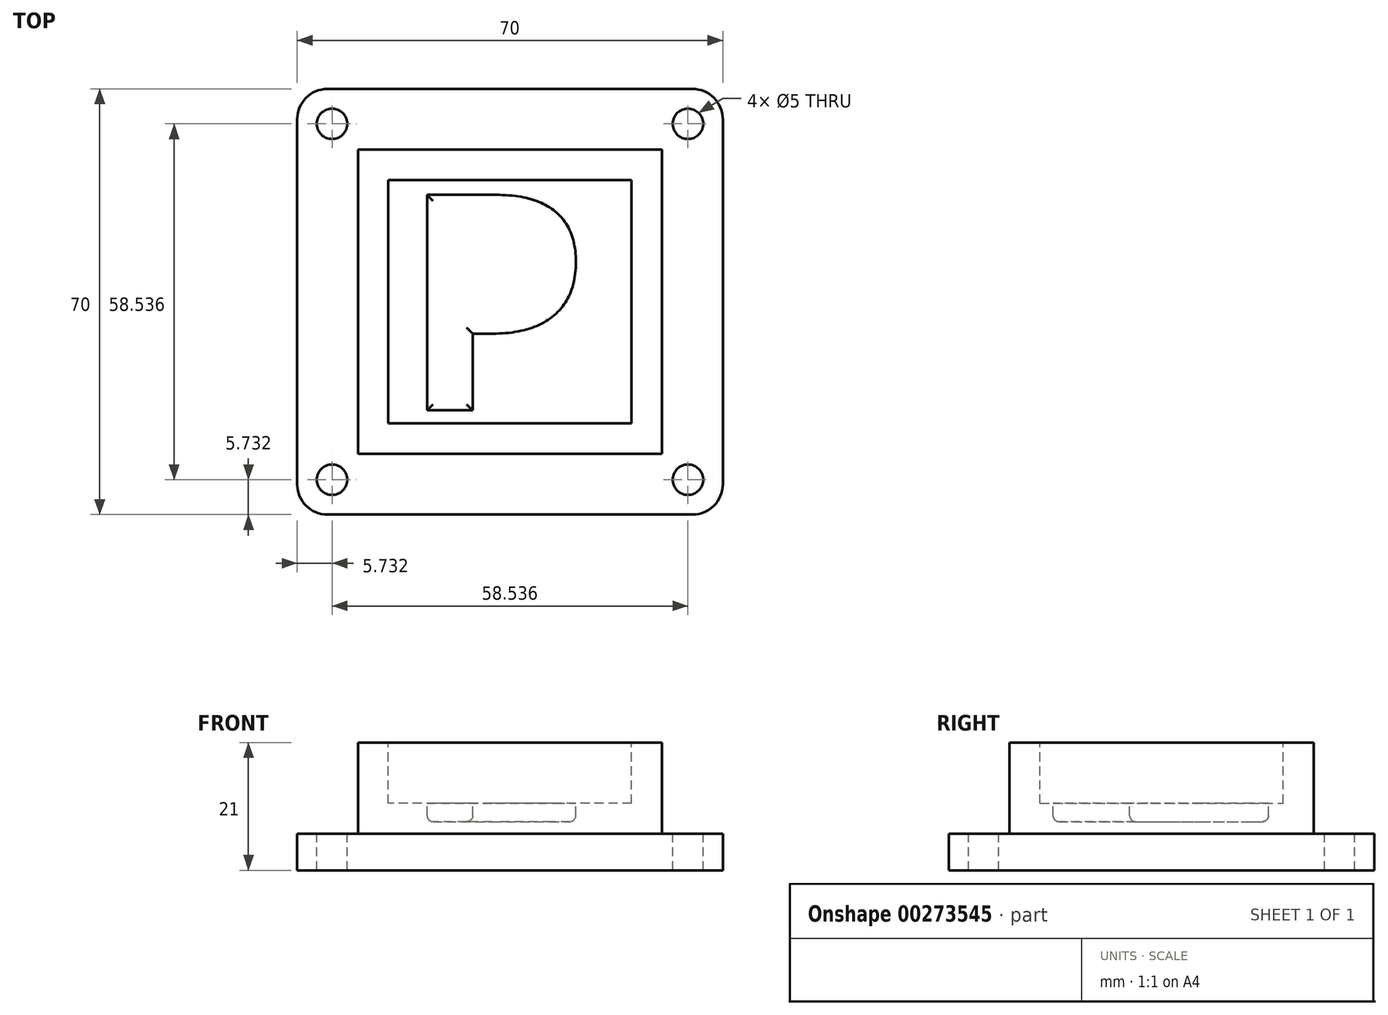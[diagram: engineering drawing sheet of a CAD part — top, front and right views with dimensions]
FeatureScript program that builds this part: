
annotation { "Feature Type Name" : "Feature", "Feature Type Description" : "" }
export const myFeature = defineFeature(function(context is Context, id is Id, definition is map)
    precondition{}
    {
        {
            var Q0;
            Q0=qCreatedBy(makeId("Top.planeOp"),FACE);
            var sketch = newSketch(context, id + "F0", { "sketchPlane" : qUnion([Q0])});
            skLineSegment(sketch, "E0.bottom", {"start": v(35, -35) * mm, "end": v(-35, -35) * mm});
            skLineSegment(sketch, "E0.top", {"start": v(35, 35) * mm, "end": v(-35, 35) * mm});
            skLineSegment(sketch, "E0.left", {"start": v(35, -35) * mm, "end": v(35, 35) * mm});
            skLineSegment(sketch, "E0.right", {"start": v(-35, -35) * mm, "end": v(-35, 35) * mm});
            skPoint(sketch, "E0.middle", {"position": v(0, 0) * mm});
            skSolve(sketch);
        }
        {
            var Q0;
            Q0=makeQuery(id+"F0.imprint","IMPRINT",FACE,{"disambiguationData":[TD([[makeQuery(id+"F0.imprint","IMPRINT",EDGE,{"derivedFrom":sQuery(id+"F0.wireOp",EDGE,"E0.bottom")}),-1.0]])]});
            extrude(context, id + "F1", {"entities" : qUnion([Q0]), "depth" : 6 * mm});
        }
        {
            var Q0;
            Q0=makeQuery(id+"F1.opExtrude","CAP_FACE",FACE,{"disambiguationData":[OSD([sQuery(id+"F0.wireOp",EDGE,"E0.bottom"),sQuery(id+"F0.wireOp",EDGE,"E0.top"),sQuery(id+"F0.wireOp",EDGE,"E0.left"),sQuery(id+"F0.wireOp",EDGE,"E0.right")])],"isStart":false});
            var sketch = newSketch(context, id + "F2", { "sketchPlane" : qUnion([Q0])});
            skLineSegment(sketch, "E1.bottom", {"start": v(25, -25) * mm, "end": v(-25, -25) * mm});
            skLineSegment(sketch, "E1.top", {"start": v(25, 25) * mm, "end": v(-25, 25) * mm});
            skLineSegment(sketch, "E1.left", {"start": v(25, -25) * mm, "end": v(25, 25) * mm});
            skLineSegment(sketch, "E1.right", {"start": v(-25, -25) * mm, "end": v(-25, 25) * mm});
            skPoint(sketch, "E1.middle", {"position": v(0, 0) * mm});
            skSolve(sketch);
        }
        {
            var Q0;
            Q0=makeQuery(id+"F2.imprint","IMPRINT",FACE,{"disambiguationData":[TD([[makeQuery(id+"F2.imprint","IMPRINT",EDGE,{"derivedFrom":sQuery(id+"F2.wireOp",EDGE,"E1.bottom")}),-1.0]])]});
            extrude(context, id + "F3", {"entities" : qUnion([Q0]), "operationType" : NewBodyOperationType.ADD, "depth" : 15 * mm});
        }
        {
            var Q0;
            Q0=makeQuery(id+"F1.opExtrude","SWEPT_EDGE",EDGE,{"disambiguationData":[OSD([sQuery(id+"F0.wireOp",EDGE,"E0.top"),sQuery(id+"F0.wireOp",EDGE,"E0.right")])]});
            var Q1;
            Q1=makeQuery(id+"F1.opExtrude","SWEPT_EDGE",EDGE,{"disambiguationData":[OSD([sQuery(id+"F0.wireOp",EDGE,"E0.top"),sQuery(id+"F0.wireOp",EDGE,"E0.left")])]});
            var Q2;
            Q2=makeQuery(id+"F1.opExtrude","SWEPT_EDGE",EDGE,{"disambiguationData":[OSD([sQuery(id+"F0.wireOp",EDGE,"E0.bottom"),sQuery(id+"F0.wireOp",EDGE,"E0.left")])]});
            var Q3;
            Q3=makeQuery(id+"F1.opExtrude","SWEPT_EDGE",EDGE,{"disambiguationData":[OSD([sQuery(id+"F0.wireOp",EDGE,"E0.bottom"),sQuery(id+"F0.wireOp",EDGE,"E0.right")])]});
            fillet(context, id + "F4", {"entities" : qUnion([Q0, Q1, Q2, Q3]), "radius" : 5 * mm, "tangentPropagation" : true, "allowEdgeOverflow" : false});
        }
        {
            var Q0;
            Q0=makeQuery(id+"F1.opExtrude","CAP_FACE",FACE,{"disambiguationData":[OSD([sQuery(id+"F0.wireOp",EDGE,"E0.bottom"),sQuery(id+"F0.wireOp",EDGE,"E0.top"),sQuery(id+"F0.wireOp",EDGE,"E0.left"),sQuery(id+"F0.wireOp",EDGE,"E0.right")])],"isStart":false});
            var sketch = newSketch(context, id + "F5", { "sketchPlane" : qUnion([Q0])});
            skLineSegment(sketch, "E2.0", {"start": v(-35, -30) * mm, "end": v(-35, 30) * mm, "construction": true});
            skPoint(sketch, "E3.0", {"position": v(-33.54, 33.54) * mm});
            skArc(sketch, "E4.0", {"start": v(-30, 35) * mm, "mid": v(-33.54, 33.54) * mm, "end": v(-35, 30) * mm});
            skLineSegment(sketch, "E5.0", {"start": v(30, 35) * mm, "end": v(-30, 35) * mm, "construction": true});
            skLineSegment(sketch, "E6.0", {"start": v(35, -30) * mm, "end": v(35, 30) * mm, "construction": true});
            skArc(sketch, "E7.0", {"start": v(30, -35) * mm, "mid": v(33.54, -33.54) * mm, "end": v(35, -30) * mm, "construction": true});
            skLineSegment(sketch, "E8.0", {"start": v(30, -35) * mm, "end": v(-30, -35) * mm, "construction": true});
            skArc(sketch, "E9.0", {"start": v(-35, -30) * mm, "mid": v(-33.54, -33.54) * mm, "end": v(-30, -35) * mm, "construction": true});
            skPoint(sketch, "E10.0", {"position": v(33.54, 33.54) * mm});
            skPoint(sketch, "E11", {"position": v(-33.54, -33.54) * mm});
            skPoint(sketch, "E12", {"position": v(33.54, -33.54) * mm});
            skLineSegment(sketch, "E13", {"start": v(-33.54, 33.54) * mm, "end": v(-25, 25) * mm, "construction": true});
            skLineSegment(sketch, "E14", {"start": v(25, 25) * mm, "end": v(33.54, 33.54) * mm, "construction": true});
            skLineSegment(sketch, "E15", {"start": v(25, -25) * mm, "end": v(33.54, -33.54) * mm, "construction": true});
            skLineSegment(sketch, "E16", {"start": v(-25, -25) * mm, "end": v(-33.54, -33.54) * mm, "construction": true});
            skPoint(sketch, "E17", {"position": v(-29.27, 29.27) * mm});
            skPoint(sketch, "E18", {"position": v(29.27, 29.27) * mm});
            skPoint(sketch, "E19", {"position": v(29.27, -29.27) * mm});
            skPoint(sketch, "E20", {"position": v(-29.27, -29.27) * mm});
            skCircle(sketch, "E21", {"center": v(-29.27, 29.27) * mm, "radius": 2.5 * mm});
            skCircle(sketch, "E22", {"center": v(29.27, 29.27) * mm, "radius": 2.5 * mm});
            skCircle(sketch, "E23", {"center": v(29.27, -29.27) * mm, "radius": 2.5 * mm});
            skCircle(sketch, "E24", {"center": v(-29.27, -29.27) * mm, "radius": 2.5 * mm});
            skSolve(sketch);
        }
        {
            var Q0;
            Q0=makeQuery(id+"F5.imprint","IMPRINT",FACE,{"disambiguationData":[TD([[makeQuery(id+"F5.imprint","IMPRINT",EDGE,{"derivedFrom":sQuery(id+"F5.wireOp",EDGE,"E21")}),1.0]])]});
            var Q1;
            Q1=makeQuery(id+"F5.imprint","IMPRINT",FACE,{"disambiguationData":[TD([[makeQuery(id+"F5.imprint","IMPRINT",EDGE,{"derivedFrom":sQuery(id+"F5.wireOp",EDGE,"E22")}),1.0]])]});
            var Q2;
            Q2=makeQuery(id+"F5.imprint","IMPRINT",FACE,{"disambiguationData":[TD([[makeQuery(id+"F5.imprint","IMPRINT",EDGE,{"derivedFrom":sQuery(id+"F5.wireOp",EDGE,"E23")}),1.0]])]});
            var Q3;
            Q3=makeQuery(id+"F5.imprint","IMPRINT",FACE,{"disambiguationData":[TD([[makeQuery(id+"F5.imprint","IMPRINT",EDGE,{"derivedFrom":sQuery(id+"F5.wireOp",EDGE,"E24")}),1.0]])]});
            extrude(context, id + "F6", {"entities" : qUnion([Q0, Q1, Q2, Q3]), "operationType" : NewBodyOperationType.REMOVE, "oppositeDirection" : true, "depth" : 25 * mm});
        }
        {
            var Q0;
            Q0=makeQuery(id+"F3.opExtrude","CAP_FACE",FACE,{"disambiguationData":[OSD([sQuery(id+"F2.wireOp",EDGE,"E1.bottom"),sQuery(id+"F2.wireOp",EDGE,"E1.top"),sQuery(id+"F2.wireOp",EDGE,"E1.left"),sQuery(id+"F2.wireOp",EDGE,"E1.right")])],"isStart":false});
            var sketch = newSketch(context, id + "F7", { "sketchPlane" : qUnion([Q0])});
            skSolve(sketch);
        }
        {
            var Q0;
            Q0=makeQuery(id+"F7.imprint","IMPRINT",FACE,{"disambiguationData":[TD([[makeQuery(id+"F7.imprint","IMPRINT",EDGE,{"derivedFrom":makeQuery(id+"F3.opExtrude","CAP_EDGE",EDGE,{"disambiguationData":[OSD([sQuery(id+"F2.wireOp",EDGE,"E1.bottom")])],"isStart":false})}),-1.0]])]});
            var sketch = newSketch(context, id + "F8", { "sketchPlane" : qUnion([Q0])});
            skLineSegment(sketch, "E25.bottom", {"start": v(20, -20) * mm, "end": v(-20, -20) * mm});
            skLineSegment(sketch, "E25.top", {"start": v(20, 20) * mm, "end": v(-20, 20) * mm});
            skLineSegment(sketch, "E25.left", {"start": v(20, -20) * mm, "end": v(20, 20) * mm});
            skLineSegment(sketch, "E25.right", {"start": v(-20, -20) * mm, "end": v(-20, 20) * mm});
            skPoint(sketch, "E25.middle", {"position": v(0, 0) * mm});
            skText(sketch, "E26", { "text": "P", "fontName": "OpenSans-Bold.ttf"});
            const initialGuessF8  = {"E26": [-0.0181, -0.01785, 1, 0, 0.03574]};
            skSetInitialGuess(sketch, initialGuessF8);
            skSolve(sketch);
        }
        {
            var Q0;
            Q0=makeQuery(id+"F8.imprint","IMPRINT",FACE,{"disambiguationData":[TD([[makeQuery(id+"F8.imprint","IMPRINT",EDGE,{"derivedFrom":sQuery(id+"F8.wireOp",EDGE,"E25.bottom")}),-1.0]])]});
            extrude(context, id + "F9", {"entities" : qUnion([Q0]), "operationType" : NewBodyOperationType.REMOVE, "oppositeDirection" : true, "depth" : 10 * mm});
        }
        {
            var Q0;
            Q0=makeQuery(id+"F8.imprint","IMPRINT",FACE,{"disambiguationData":[TD([[makeQuery(id+"F8.imprint","IMPRINT",EDGE,{"derivedFrom":sQuery(id+"F8.wireOp",EDGE,"E26.sketch_text.stroke-0")}),-1.0]])]});
            extrude(context, id + "F10", {"entities" : qUnion([Q0]), "operationType" : NewBodyOperationType.REMOVE, "oppositeDirection" : true, "depth" : 13 * mm});
        }
        {
            var Q0;
            Q0=makeQuery(id+"F8.imprint","IMPRINT",FACE,{"disambiguationData":[TD([[makeQuery(id+"F8.imprint","IMPRINT",EDGE,{"derivedFrom":sQuery(id+"F8.wireOp",EDGE,"E26.sketch_text.stroke-0")}),1.0]])]});
            extrude(context, id + "F11", {"entities" : qUnion([Q0]), "operationType" : NewBodyOperationType.REMOVE, "oppositeDirection" : true, "depth" : 13 * mm});
        }
        {
            var Q0;
            Q0=makeQuery(id+"F10.boolean.opBoolean","COPY",EDGE,{"derivedFrom":makeQuery(id+"F10.opExtrude","CAP_EDGE",EDGE,{"disambiguationData":[OSD([sQuery(id+"F8.wireOp",EDGE,"E26.sketch_text.stroke-12")])],"isStart":false})});
            var Q1;
            Q1=makeQuery(id+"F10.boolean.opBoolean","COPY",EDGE,{"derivedFrom":makeQuery(id+"F10.opExtrude","CAP_EDGE",EDGE,{"disambiguationData":[OSD([sQuery(id+"F8.wireOp",EDGE,"E26.sketch_text.stroke-13")])],"isStart":false})});
            var Q2;
            Q2=makeQuery(id+"F10.boolean.opBoolean","COPY",EDGE,{"derivedFrom":makeQuery(id+"F10.opExtrude","CAP_EDGE",EDGE,{"disambiguationData":[OSD([sQuery(id+"F8.wireOp",EDGE,"E26.sketch_text.stroke-14")])],"isStart":false})});
            var Q3;
            Q3=makeQuery(id+"F10.boolean.opBoolean","COPY",EDGE,{"derivedFrom":makeQuery(id+"F10.opExtrude","CAP_EDGE",EDGE,{"disambiguationData":[OSD([sQuery(id+"F8.wireOp",EDGE,"E26.sketch_text.stroke-15")])],"isStart":false})});
            var Q4;
            Q4=makeQuery(id+"F10.boolean.opBoolean","COPY",EDGE,{"derivedFrom":makeQuery(id+"F10.opExtrude","CAP_EDGE",EDGE,{"disambiguationData":[OSD([sQuery(id+"F8.wireOp",EDGE,"E26.sketch_text.stroke-7")])],"isStart":false})});
            var Q5;
            Q5=makeQuery(id+"F10.boolean.opBoolean","COPY",EDGE,{"derivedFrom":makeQuery(id+"F10.opExtrude","CAP_EDGE",EDGE,{"disambiguationData":[OSD([sQuery(id+"F8.wireOp",EDGE,"E26.sketch_text.stroke-8")])],"isStart":false})});
            var Q6;
            Q6=makeQuery(id+"F10.boolean.opBoolean","COPY",EDGE,{"derivedFrom":makeQuery(id+"F10.opExtrude","CAP_EDGE",EDGE,{"disambiguationData":[OSD([sQuery(id+"F8.wireOp",EDGE,"E26.sketch_text.stroke-9")])],"isStart":false})});
            var Q7;
            Q7=makeQuery(id+"F10.boolean.opBoolean","COPY",EDGE,{"derivedFrom":makeQuery(id+"F10.opExtrude","CAP_EDGE",EDGE,{"disambiguationData":[OSD([sQuery(id+"F8.wireOp",EDGE,"E26.sketch_text.stroke-10")])],"isStart":false})});
            var Q8;
            Q8=makeQuery(id+"F10.boolean.opBoolean","COPY",EDGE,{"derivedFrom":makeQuery(id+"F10.opExtrude","CAP_EDGE",EDGE,{"disambiguationData":[OSD([sQuery(id+"F8.wireOp",EDGE,"E26.sketch_text.stroke-11")])],"isStart":false})});
            fillet(context, id + "F12", {"entities" : qUnion([Q0, Q1, Q2, Q3, Q4, Q5, Q6, Q7, Q8]), "radius" : 1 * mm, "tangentPropagation" : true, "allowEdgeOverflow" : false});
        }
    });
